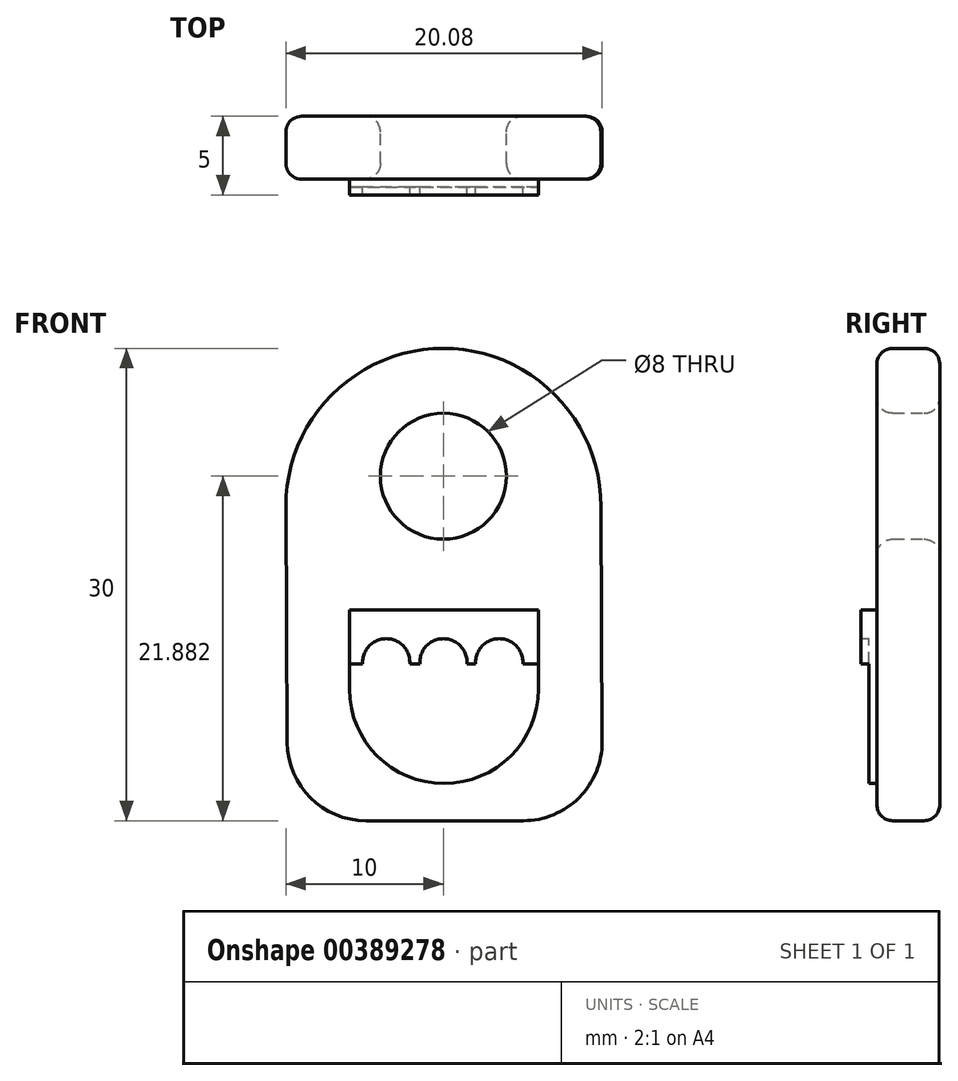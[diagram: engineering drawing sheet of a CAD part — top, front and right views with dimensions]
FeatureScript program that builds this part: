
annotation { "Feature Type Name" : "Feature", "Feature Type Description" : "" }
export const myFeature = defineFeature(function(context is Context, id is Id, definition is map)
    precondition{}
    {
        {
            var Q0;
            Q0=qCreatedBy(makeId("Front.planeOp"),FACE);
            var sketch = newSketch(context, id + "F0", { "sketchPlane" : qUnion([Q0])});
            skLineSegment(sketch, "E0.bottom", {"start": v(0, 0) * mm, "end": v(-20, 0) * mm});
            skLineSegment(sketch, "E0.left", {"start": v(0, 0) * mm, "end": v(-0.1, 19.97) * mm});
            skLineSegment(sketch, "E0.right", {"start": v(-20, 0) * mm, "end": v(-20.1, 19.94) * mm});
            skArc(sketch, "E1", {"start": v(-0.1, 19.97) * mm, "mid": v(-10.12, 30) * mm, "end": v(-20.1, 19.94) * mm});
            skLineSegment(sketch, "E2", {"start": v(-10.12, 30) * mm, "end": v(-53.87, 30) * mm, "construction": true});
            skCircle(sketch, "E3", {"center": v(-10.1, 21.88) * mm, "radius": 4 * mm});
            skSolve(sketch);
        }
        {
            var Q0;
            Q0 = qSketchRegion(id + "F0", true);
            extrude(context, id + "F1", {"entities" : qUnion([Q0]), "depth" : 4 * mm, "offsetDistance" : 25 * mm});
        }
        {
            var Q0;
            Q0=makeQuery(id+"F1.opExtrude","CAP_FACE",FACE,{"disambiguationData":[OSD([sQuery(id+"F0.wireOp",EDGE,"E0.bottom"),sQuery(id+"F0.wireOp",EDGE,"E0.left"),sQuery(id+"F0.wireOp",EDGE,"E0.right"),sQuery(id+"F0.wireOp",EDGE,"E1"),sQuery(id+"F0.wireOp",EDGE,"E3")])],"isStart":false});
            var sketch = newSketch(context, id + "F2", { "sketchPlane" : qUnion([Q0])});
            skLineSegment(sketch, "E4.bottom", {"start": v(-16.07, 13.4) * mm, "end": v(-4.07, 13.4) * mm});
            skLineSegment(sketch, "E4.left", {"start": v(-16.07, 13.4) * mm, "end": v(-16.07, 8.36) * mm});
            skLineSegment(sketch, "E4.right", {"start": v(-4.07, 13.4) * mm, "end": v(-4.07, 8.36) * mm});
            skArc(sketch, "E5", {"start": v(-16.07, 8.36) * mm, "mid": v(-10.07, 2.36) * mm, "end": v(-4.07, 8.36) * mm});
            skArc(sketch, "E6", {"start": v(-12.24, 9.97) * mm, "mid": v(-13.74, 11.56) * mm, "end": v(-15.24, 9.97) * mm});
            skArc(sketch, "E7", {"start": v(-8.61, 9.97) * mm, "mid": v(-10.11, 11.56) * mm, "end": v(-11.6, 9.97) * mm});
            skArc(sketch, "E8", {"start": v(-5.06, 9.97) * mm, "mid": v(-6.56, 11.56) * mm, "end": v(-8.06, 9.97) * mm});
            skLineSegment(sketch, "E9", {"start": v(-16.07, 9.97) * mm, "end": v(-15.24, 9.97) * mm});
            skPoint(sketch, "E9.startSnap0", {"position": v(-20.05, 9.97) * mm});
            skLineSegment(sketch, "E10", {"start": v(-12.24, 9.97) * mm, "end": v(-11.6, 9.97) * mm});
            skLineSegment(sketch, "E11", {"start": v(-8.61, 9.97) * mm, "end": v(-8.06, 9.97) * mm});
            skLineSegment(sketch, "E12", {"start": v(-5.06, 9.97) * mm, "end": v(-4.07, 9.97) * mm});
            skSolve(sketch);
        }
        {
            var Q0;
            Q0 = qSketchRegion(id + "F2", true);
            extrude(context, id + "F3", {"entities" : qUnion([Q0]), "operationType" : NewBodyOperationType.ADD, "depth" : 0.5 * mm, "offsetDistance" : 25 * mm});
        }
        {
            var Q0;
            {var subQ1=sQuery(id+"F2.wireOp",EDGE,"E4.bottom");Q0=makeQuery(id+"F2.imprint","IMPRINT",FACE,{"disambiguationData":[TD([[makeQuery(id+"F2.imprint","IMPRINT",EDGE,{"derivedFrom":subQ1}),-1.0]])]});}
            extrude(context, id + "F4", {"entities" : qUnion([Q0]), "operationType" : NewBodyOperationType.ADD, "depth" : 1 * mm, "offsetDistance" : 25 * mm});
        }
        {
            var Q0;
            Q0=makeQuery(id+"F1.opExtrude","SWEPT_EDGE",EDGE,{"disambiguationData":[OSD([sQuery(id+"F0.wireOp",EDGE,"E0.bottom"),sQuery(id+"F0.wireOp",EDGE,"E0.left")])]});
            var Q1;
            Q1=makeQuery(id+"F1.opExtrude","SWEPT_EDGE",EDGE,{"disambiguationData":[OSD([sQuery(id+"F0.wireOp",EDGE,"E0.bottom"),sQuery(id+"F0.wireOp",EDGE,"E0.right")])]});
            fillet(context, id + "F5", {"entities" : qUnion([Q0, Q1]), "radius" : 5 * mm, "tangentPropagation" : true, "allowEdgeOverflow" : false});
        }
        {
            var Q0;
            Q0=makeQuery(id+"F1.opExtrude","CAP_EDGE",EDGE,{"disambiguationData":[OSD([sQuery(id+"F0.wireOp",EDGE,"E3")])],"isStart":false});
            var Q1;
            Q1=makeQuery(id+"F1.opExtrude","CAP_EDGE",EDGE,{"disambiguationData":[OSD([sQuery(id+"F0.wireOp",EDGE,"E3")])],"isStart":true});
            fillet(context, id + "F6", {"entities" : qUnion([Q0, Q1]), "radius" : 1 * mm, "tangentPropagation" : true, "allowEdgeOverflow" : false});
        }
        {
            var Q0;
            Q0=makeQuery(id+"F1.opExtrude","CAP_EDGE",EDGE,{"disambiguationData":[OSD([sQuery(id+"F0.wireOp",EDGE,"E0.right")])],"isStart":false});
            var Q1;
            Q1=makeQuery(id+"F1.opExtrude","CAP_EDGE",EDGE,{"disambiguationData":[OSD([sQuery(id+"F0.wireOp",EDGE,"E0.right")])],"isStart":true});
            fillet(context, id + "F7", {"entities" : qUnion([Q0, Q1]), "radius" : 1 * mm, "tangentPropagation" : true, "allowEdgeOverflow" : false});
        }
    });
